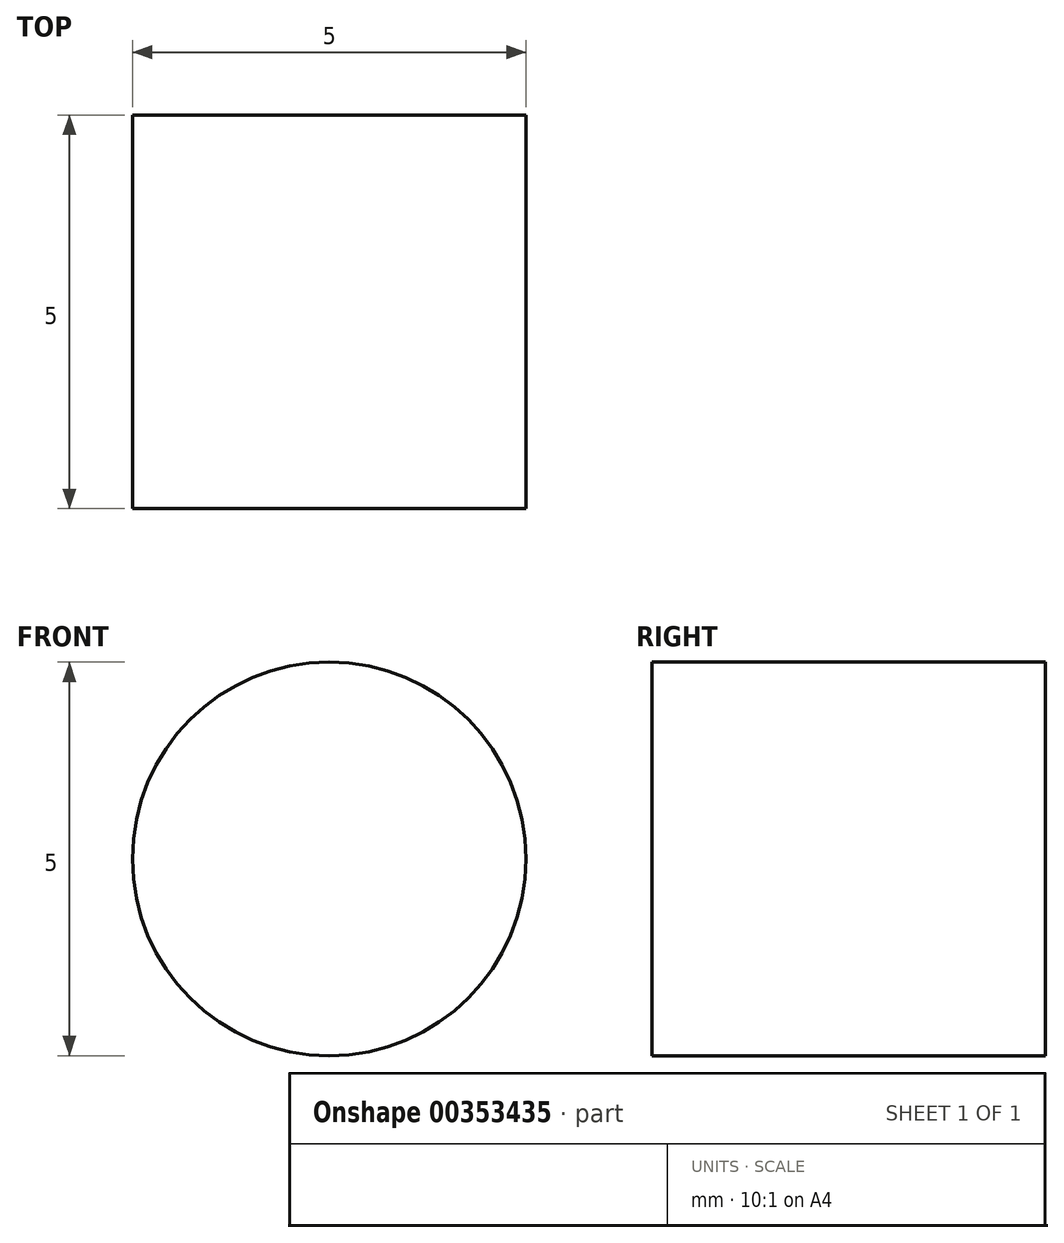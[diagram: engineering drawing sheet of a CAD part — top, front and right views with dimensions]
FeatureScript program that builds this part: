
annotation { "Feature Type Name" : "Feature", "Feature Type Description" : "" }
export const myFeature = defineFeature(function(context is Context, id is Id, definition is map)
    precondition{}
    {
        {
            var Q0;
            Q0=qCreatedBy(makeId("Front.planeOp"),FACE);
            var sketch = newSketch(context, id + "F0", { "sketchPlane" : qUnion([Q0])});
            skCircle(sketch, "E0", {"center": v(0, 0) * mm, "radius": 2.5 * mm});
            skSolve(sketch);
        }
        {
            var Q0;
            Q0=makeQuery(id+"F0.imprint","IMPRINT",FACE,{"disambiguationData":[TD([[makeQuery(id+"F0.imprint","IMPRINT",EDGE,{"derivedFrom":sQuery(id+"F0.wireOp",EDGE,"E0")}),1.0]])]});
            extrude(context, id + "F1", {"entities" : qUnion([Q0]), "endBound" : BoundingType.SYMMETRIC, "depth" : 5 * mm});
        }
    });
